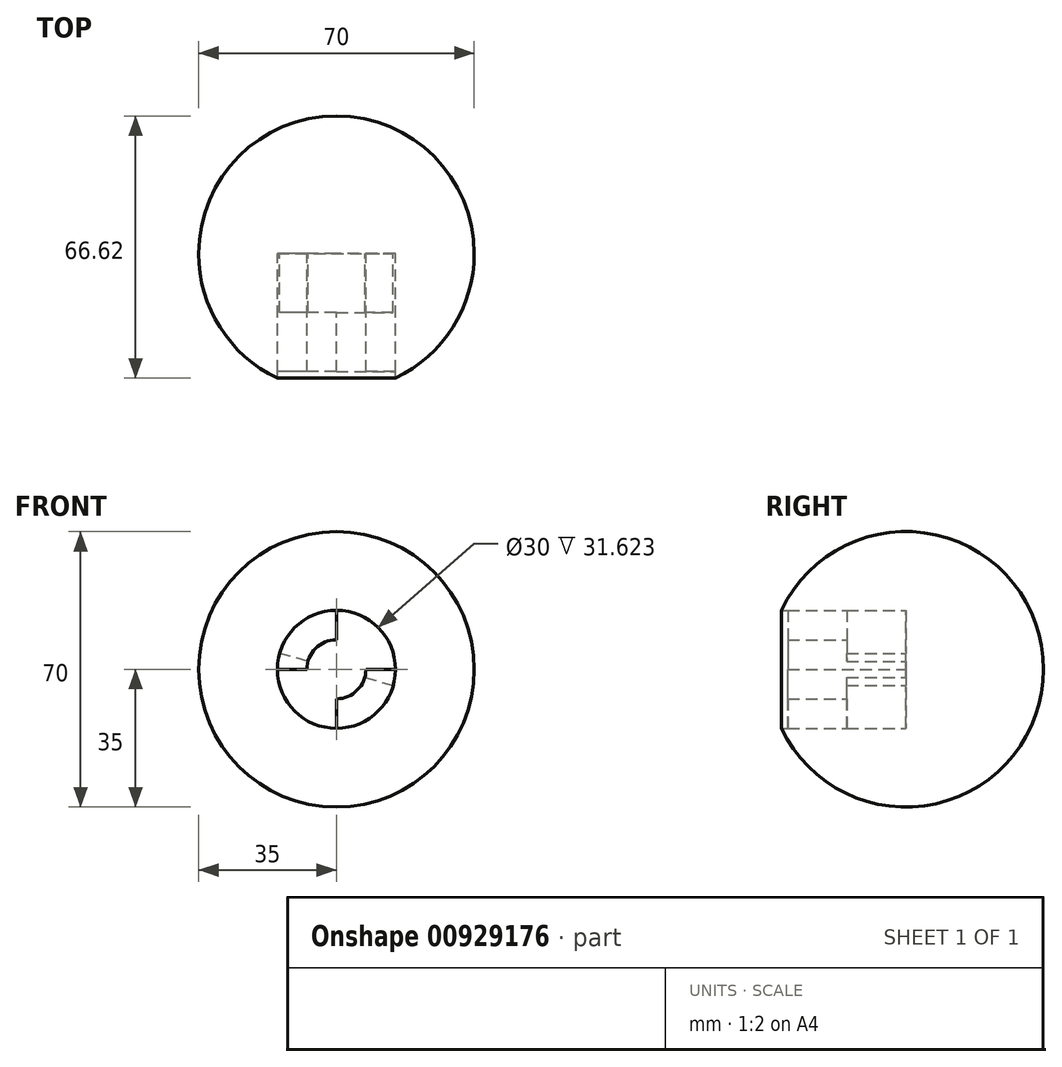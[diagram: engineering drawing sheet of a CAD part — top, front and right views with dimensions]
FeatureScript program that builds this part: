
annotation { "Feature Type Name" : "Feature", "Feature Type Description" : "" }
export const myFeature = defineFeature(function(context is Context, id is Id, definition is map)
    precondition{}
    {
        {
            var Q0;
            Q0=qCreatedBy(makeId("Top.planeOp"),FACE);
            var sketch = newSketch(context, id + "F0", { "sketchPlane" : qUnion([Q0])});
            skArc(sketch, "E0", {"start": v(-35, 0) * mm, "mid": v(0, -35) * mm, "end": v(35, 0) * mm});
            skLineSegment(sketch, "E1", {"start": v(-35, 0) * mm, "end": v(35, 0) * mm});
            skSolve(sketch);
        }
        {
            var Q0;
            Q0=qCreatedBy(makeId("Front.planeOp"),FACE);
            var sketch = newSketch(context, id + "F1", { "sketchPlane" : qUnion([Q0])});
            skCircle(sketch, "E2", {"center": v(0, 0) * mm, "radius": 15 * mm});
            skArc(sketch, "E3", {"start": v(0, -7.5) * mm, "mid": v(5.3, -5.3) * mm, "end": v(7.5, 0) * mm});
            skLineSegment(sketch, "E4", {"start": v(0, 15) * mm, "end": v(0, 7.5) * mm});
            skLineSegment(sketch, "E5", {"start": v(15, 0) * mm, "end": v(7.5, 0) * mm});
            skLineSegment(sketch, "E6.trimOffspring", {"start": v(0, -7.5) * mm, "end": v(0, -15) * mm});
            skLineSegment(sketch, "E7.trimOffspring", {"start": v(-7.5, 0) * mm, "end": v(-15, 0) * mm});
            skArc(sketch, "E8.trimOffspring", {"start": v(0, 7.5) * mm, "mid": v(-5.3, 5.3) * mm, "end": v(-7.5, 0) * mm});
            skLineSegment(sketch, "E9", {"start": v(0, 0) * mm, "end": v(-14.43, 4.1) * mm});
            skLineSegment(sketch, "E10", {"start": v(-14.43, 4.1) * mm, "end": v(14.43, -4.1) * mm});
            skSolve(sketch);
        }
        {
            var Q0;
            Q0=makeQuery(id+"F0.imprint","IMPRINT",FACE,{"disambiguationData":[TD([[makeQuery(id+"F0.imprint","IMPRINT",EDGE,{"derivedFrom":sQuery(id+"F0.wireOp",EDGE,"E0")}),1.0]])]});
            var Q1;
            Q1=sQuery(id+"F0.wireOp",EDGE,"E1");
            revolve(context, id + "F2", {"surfaceOperationType" : NewSurfaceOperationType.NEW, "entities" : qUnion([Q0]), "axis" : qUnion([Q1]), "revolveType" : RevolveType.FULL});
        }
        {
            var Q0;
            Q0 = qSketchRegion(id + "F1", true);
            extrude(context, id + "F3", {"entities" : qUnion([Q0]), "operationType" : NewBodyOperationType.REMOVE, "depth" : 100 * mm, "offsetDistance" : 25 * mm});
        }
        {
            var Q0;
            {var subQ0=sQuery(id+"F1.wireOp",EDGE,"E4");Q0=makeQuery(id+"F1.imprint","IMPRINT",FACE,{"disambiguationData":[TD([[makeQuery(id+"F1.imprint","IMPRINT",EDGE,{"derivedFrom":subQ0}),-1.0]])]});}
            var Q1;
            Q1=makeQuery(id+"F1.imprint","IMPRINT",FACE,{"disambiguationData":[TD([[makeQuery(id+"F1.imprint","IMPRINT",EDGE,{"derivedFrom":sQuery(id+"F1.wireOp",EDGE,"E3")}),-1.0]])]});
            extrude(context, id + "F4", {"entities" : qUnion([Q0, Q1]), "operationType" : NewBodyOperationType.ADD, "depth" : 30 * mm, "offsetDistance" : 25 * mm});
        }
        {
            var Q0;
            {var subQ0=sQuery(id+"F1.wireOp",EDGE,"E4");Q0=makeQuery(id+"F1.imprint","IMPRINT",FACE,{"disambiguationData":[TD([[makeQuery(id+"F1.imprint","IMPRINT",EDGE,{"derivedFrom":subQ0}),-1.0]])]});}
            var Q1;
            Q1=makeQuery(id+"F1.imprint","IMPRINT",FACE,{"disambiguationData":[TD([[makeQuery(id+"F1.imprint","IMPRINT",EDGE,{"derivedFrom":sQuery(id+"F1.wireOp",EDGE,"E3")}),-1.0]])]});
            extrude(context, id + "F5", {"entities" : qUnion([Q0, Q1]), "operationType" : NewBodyOperationType.REMOVE, "depth" : 15 * mm, "offsetDistance" : 25 * mm});
        }
        {
            var Q0;
            {var subQ0=sQuery(id+"F1.wireOp",EDGE,"E7.trimOffspring");Q0=makeQuery(id+"F1.imprint","IMPRINT",FACE,{"disambiguationData":[TD([[makeQuery(id+"F1.imprint","IMPRINT",EDGE,{"derivedFrom":subQ0}),-1.0]])]});}
            var Q1;
            {var subQ0=sQuery(id+"F1.wireOp",EDGE,"E5");Q1=makeQuery(id+"F1.imprint","IMPRINT",FACE,{"disambiguationData":[TD([[makeQuery(id+"F1.imprint","IMPRINT",EDGE,{"derivedFrom":subQ0}),1.0]])]});}
            extrude(context, id + "F6", {"entities" : qUnion([Q0, Q1]), "operationType" : NewBodyOperationType.ADD, "depth" : 30 * mm, "offsetDistance" : 25 * mm});
        }
    });
